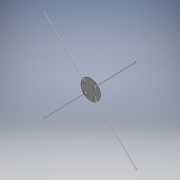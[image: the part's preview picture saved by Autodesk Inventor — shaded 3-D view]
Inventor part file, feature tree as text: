
AUTODESK INVENTOR PART (.ipt)
format: ipt  version: 2016 (Build 200138000, 138)  size: 123,392 bytes
history: native  units: mm
features: extrude x3, sketch x3, pattern_circular x1
ambient origin geometry x8: Origin, YZ Plane, XZ Plane, XY Plane, X Axis, Y Axis, Z Axis, Center Point
bodies: Solid1 (feature_tree)
feature tree (7):
  extrude  "Extrusion1"  Depth=1.0mm TaperAngle=0.0deg
  extrude  "Extrusion2"  Depth=10.0mm
  extrude  "Extrusion3"  Depth=418.75mm TaperAngle=360.0deg
  pattern_circular  "Circular Pattern1"  [2 undecoded]
  sketch  "Sketch1"  dims[d0=140.0mm d1=1.0mm d2=0.0mm]
  sketch  "Sketch2"  dims[d3=10.0mm d4=0.0mm d5=5.0mm]
  sketch  "Sketch3"  dims[d6=418.75mm d7=0.0mm d8=40.0mm d9=360.0deg]
note: 2 required parameter values undecoded (feature->parameter linkage not recoverable at this tier; creation-order binding heuristic only, values carry confidence <= 0.55)
